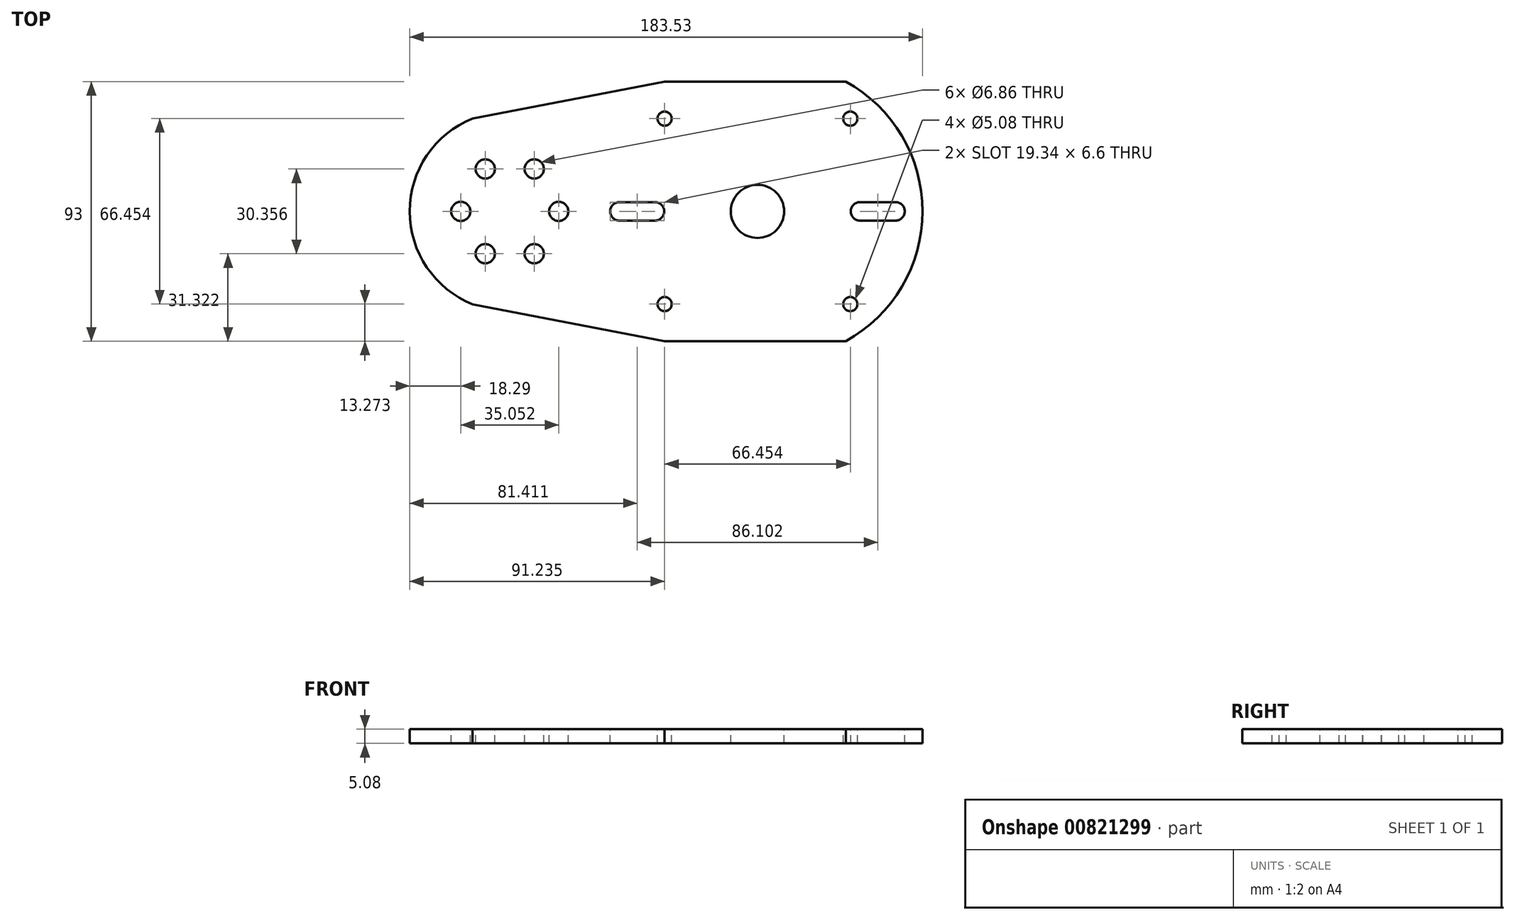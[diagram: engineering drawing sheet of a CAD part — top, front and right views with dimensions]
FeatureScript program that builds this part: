
annotation { "Feature Type Name" : "Feature", "Feature Type Description" : "" }
export const myFeature = defineFeature(function(context is Context, id is Id, definition is map)
    precondition{}
    {
        {
            var Q0;
            Q0=qCreatedBy(makeId("Top.planeOp"),FACE);
            var sketch = newSketch(context, id + "F0", { "sketchPlane" : qUnion([Q0])});
            skLineSegment(sketch, "E0", {"start": v(0, 0) * mm, "end": v(-58.93, 0) * mm, "construction": true});
            skPoint(sketch, "E1", {"position": v(-29.46, 0) * mm});
            skCircle(sketch, "E2", {"center": v(-29.46, 0) * mm, "radius": 29.46 * mm, "construction": true});
            skCircle(sketch, "E3", {"center": v(-29.46, 0) * mm, "radius": 17.53 * mm, "construction": true});
            skPoint(sketch, "E4", {"position": v(59.18, 0) * mm});
            skPoint(sketch, "E5", {"position": v(-11.94, 0) * mm});
            skCircle(sketch, "E6", {"center": v(59.18, 0) * mm, "radius": 19.05 * mm, "construction": true});
            skCircle(sketch, "E7", {"center": v(59.18, 0) * mm, "radius": 31.75 * mm, "construction": true});
            skCircle(sketch, "E8", {"center": v(-11.94, 0) * mm, "radius": 3.43 * mm});
            skCircle(sketch, "E9.1.0", {"center": v(-20.7, 15.18) * mm, "radius": 3.43 * mm});
            skCircle(sketch, "E9.2.0", {"center": v(-38.23, 15.18) * mm, "radius": 3.43 * mm});
            skCircle(sketch, "E9.3.0", {"center": v(-46.99, 0) * mm, "radius": 3.43 * mm});
            skCircle(sketch, "E9.4.0", {"center": v(-38.23, -15.18) * mm, "radius": 3.43 * mm});
            skCircle(sketch, "E9.5.0", {"center": v(-20.7, -15.18) * mm, "radius": 3.43 * mm});
            skCircle(sketch, "E10", {"center": v(-29.46, 0) * mm, "radius": 10.16 * mm, "construction": true});
            skCircle(sketch, "E11", {"center": v(-29.46, 0) * mm, "radius": 35.81 * mm, "construction": true});
            skArc(sketch, "E12", {"start": v(92.4, -46.5) * mm, "mid": v(116.33, 0) * mm, "end": v(92.4, 46.5) * mm, "construction": true});
            skPoint(sketch, "E13", {"position": v(-29.46, 35.81) * mm});
            skPoint(sketch, "E14", {"position": v(-29.46, -35.81) * mm});
            skPoint(sketch, "E15", {"position": v(59.18, 57.15) * mm});
            skPoint(sketch, "E16", {"position": v(59.18, -57.15) * mm});
            skPoint(sketch, "E17", {"position": v(-65.28, 0) * mm});
            skArc(sketch, "E18", {"start": v(-42.78, 33.25) * mm, "mid": v(-65.28, 0) * mm, "end": v(-42.78, -33.25) * mm});
            skLineSegment(sketch, "E19", {"start": v(90.93, 0) * mm, "end": v(118.25, 0) * mm, "construction": true});
            skCircle(sketch, "E20", {"center": v(59.18, 0) * mm, "radius": 47 * mm, "construction": true});
            skLineSegment(sketch, "E21", {"start": v(59.18, 0) * mm, "end": v(90.93, 0) * mm, "construction": true});
            skLineSegment(sketch, "E22", {"start": v(59.18, 0) * mm, "end": v(99.6, 40.41) * mm, "construction": true});
            skCircle(sketch, "E23", {"center": v(92.4, 33.23) * mm, "radius": 2.54 * mm});
            skCircle(sketch, "E24.2.0", {"center": v(25.96, 33.23) * mm, "radius": 2.54 * mm});
            skCircle(sketch, "E25", {"center": v(59.18, 0) * mm, "radius": 9.53 * mm});
            skCircle(sketch, "E26.1.4.0", {"center": v(25.96, -33.23) * mm, "radius": 2.54 * mm});
            skCircle(sketch, "E26.1.6.0", {"center": v(92.4, -33.23) * mm, "radius": 2.54 * mm});
            skPoint(sketch, "E27", {"position": v(25.96, 46.5) * mm});
            skPoint(sketch, "E28", {"position": v(25.96, -46.5) * mm});
            skLineSegment(sketch, "E29", {"start": v(25.96, 46.5) * mm, "end": v(-42.78, 33.25) * mm});
            skLineSegment(sketch, "E30", {"start": v(25.96, -46.5) * mm, "end": v(-42.78, -33.25) * mm});
            skLineSegment(sketch, "E31", {"start": v(25.96, 46.5) * mm, "end": v(90.78, 46.5) * mm});
            skLineSegment(sketch, "E32", {"start": v(25.96, -46.5) * mm, "end": v(90.78, -46.5) * mm});
            skArc(sketch, "E33.converted", {"start": v(92.4, 46.5) * mm, "mid": v(2.03, 0) * mm, "end": v(92.4, -46.5) * mm, "construction": true});
            skLineSegment(sketch, "E34", {"start": v(59.18, 0) * mm, "end": v(99.6, -40.41) * mm, "construction": true});
            skArc(sketch, "E35", {"start": v(90.78, -46.5) * mm, "mid": v(118.25, 0) * mm, "end": v(90.78, 46.5) * mm});
            skCircle(sketch, "E36", {"center": v(59.18, 0) * mm, "radius": 36.83 * mm, "construction": true});
            skCircle(sketch, "E37", {"center": v(59.18, 0) * mm, "radius": 49.53 * mm, "construction": true});
            skLineSegment(sketch, "E38", {"start": v(95.86, 3.3) * mm, "end": v(108.6, 3.3) * mm});
            skLineSegment(sketch, "E39", {"start": v(95.86, -3.3) * mm, "end": v(108.6, -3.3) * mm});
            skArc(sketch, "E40", {"start": v(108.6, 3.3) * mm, "mid": v(111.9, 0) * mm, "end": v(108.6, -3.3) * mm});
            skArc(sketch, "E41", {"start": v(95.86, 3.3) * mm, "mid": v(92.56, 0) * mm, "end": v(95.86, -3.3) * mm});
            skLineSegment(sketch, "E42.1.0", {"start": v(22.5, -3.3) * mm, "end": v(9.76, -3.3) * mm});
            skArc(sketch, "E42.1.1", {"start": v(22.5, -3.3) * mm, "mid": v(25.8, 0) * mm, "end": v(22.5, 3.3) * mm});
            skLineSegment(sketch, "E42.1.2", {"start": v(22.5, 3.3) * mm, "end": v(9.76, 3.3) * mm});
            skArc(sketch, "E42.1.3", {"start": v(9.76, -3.3) * mm, "mid": v(6.46, 0) * mm, "end": v(9.76, 3.3) * mm});
            skSolve(sketch);
        }
        {
            var Q0;
            Q0=makeQuery(id+"F0.imprint","IMPRINT",FACE,{"disambiguationData":[TD([[makeQuery(id+"F0.imprint","IMPRINT",EDGE,{"derivedFrom":sQuery(id+"F0.wireOp",EDGE,"E8")}),-1.0]])]});
            extrude(context, id + "F1", {"entities" : qUnion([Q0]), "oppositeDirection" : true, "depth" : 5.08 * mm, "offsetDistance" : 25.4 * mm});
        }
    });
